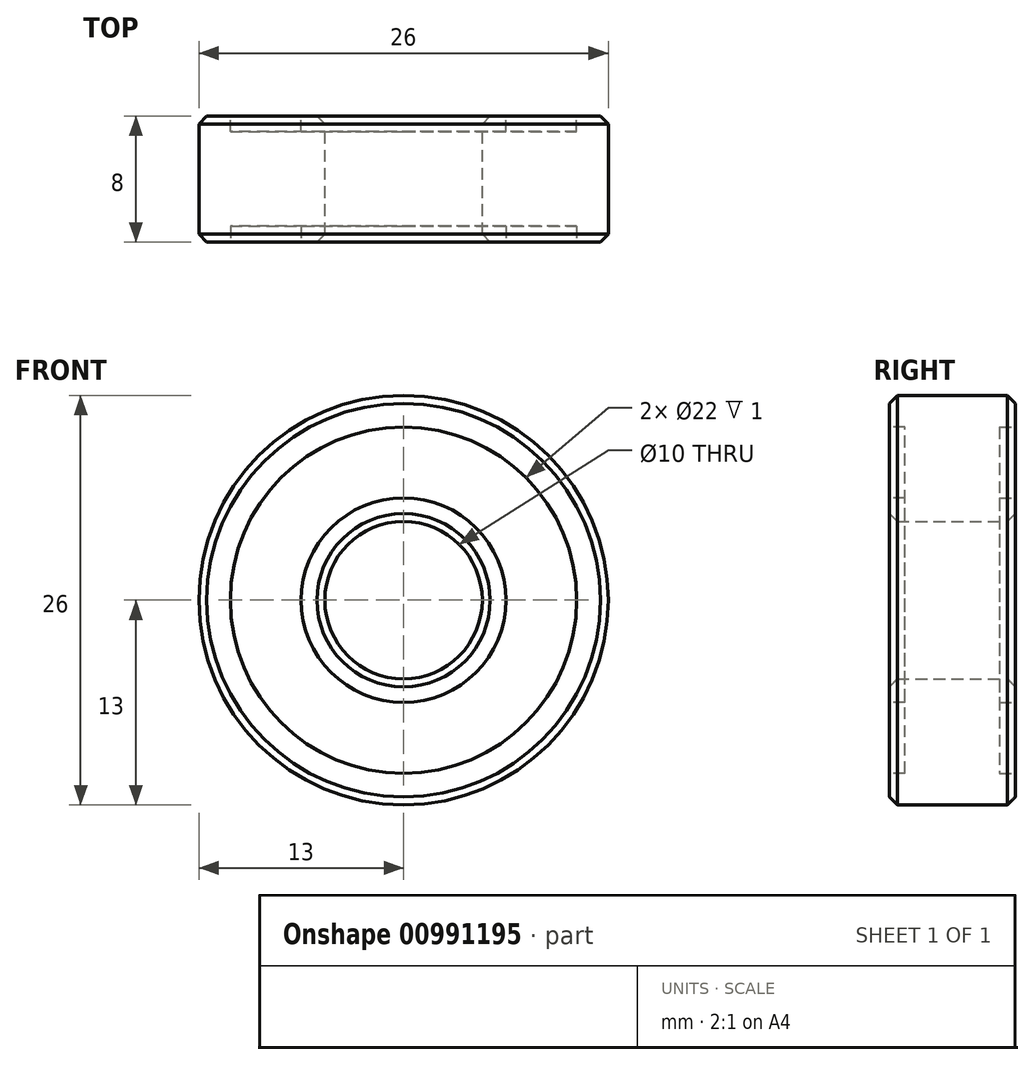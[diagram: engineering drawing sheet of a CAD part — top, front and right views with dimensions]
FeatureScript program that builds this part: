
annotation { "Feature Type Name" : "Feature", "Feature Type Description" : "" }
export const myFeature = defineFeature(function(context is Context, id is Id, definition is map)
    precondition{}
    {
        {
            var Q0;
            Q0=qCreatedBy(makeId("Front.planeOp"),FACE);
            var sketch = newSketch(context, id + "F0", { "sketchPlane" : qUnion([Q0])});
            skCircle(sketch, "E0", {"center": v(0, 0) * mm, "radius": 5 * mm});
            skCircle(sketch, "E1", {"center": v(0, 0) * mm, "radius": 13 * mm});
            skSolve(sketch);
        }
        {
            var Q0;
            Q0=makeQuery(id+"F0.imprint","IMPRINT",FACE,{"disambiguationData":[TD([[makeQuery(id+"F0.imprint","IMPRINT",EDGE,{"derivedFrom":sQuery(id+"F0.wireOp",EDGE,"E0")}),-1.0]])]});
            extrude(context, id + "F1", {"entities" : qUnion([Q0]), "depth" : 8 * mm, "offsetDistance" : 25 * mm, "symmetric" : true});
        }
        {
            var Q0;
            Q0=makeQuery(id+"F1.opExtrude","CAP_FACE",FACE,{"disambiguationData":[OSD([sQuery(id+"F0.wireOp",EDGE,"E0"),sQuery(id+"F0.wireOp",EDGE,"E1")])],"isStart":true});
            var sketch = newSketch(context, id + "F2", { "sketchPlane" : qUnion([Q0])});
            skCircle(sketch, "E2", {"center": v(0, 0) * mm, "radius": 6.5 * mm});
            skCircle(sketch, "E3", {"center": v(0, 0) * mm, "radius": 11 * mm});
            skSolve(sketch);
        }
        {
            var Q0;
            Q0=makeQuery(id+"F1.opExtrude","CAP_FACE",FACE,{"disambiguationData":[OSD([sQuery(id+"F0.wireOp",EDGE,"E0"),sQuery(id+"F0.wireOp",EDGE,"E1")])],"isStart":false});
            var sketch = newSketch(context, id + "F3", { "sketchPlane" : qUnion([Q0])});
            skCircle(sketch, "E4", {"center": v(0, 0) * mm, "radius": 6.5 * mm});
            skCircle(sketch, "E5", {"center": v(0, 0) * mm, "radius": 11 * mm});
            skSolve(sketch);
        }
        {
            var Q0;
            Q0=makeQuery(id+"F2.imprint","IMPRINT",FACE,{"disambiguationData":[TD([[makeQuery(id+"F2.imprint","IMPRINT",EDGE,{"derivedFrom":sQuery(id+"F2.wireOp",EDGE,"E2")}),-1.0]])]});
            extrude(context, id + "F4", {"entities" : qUnion([Q0]), "operationType" : NewBodyOperationType.REMOVE, "oppositeDirection" : true, "depth" : 1 * mm, "offsetDistance" : 25 * mm});
        }
        {
            var Q0;
            Q0=makeQuery(id+"F3.imprint","IMPRINT",FACE,{"disambiguationData":[TD([[makeQuery(id+"F3.imprint","IMPRINT",EDGE,{"derivedFrom":sQuery(id+"F3.wireOp",EDGE,"E4")}),-1.0]])]});
            extrude(context, id + "F5", {"entities" : qUnion([Q0]), "operationType" : NewBodyOperationType.REMOVE, "oppositeDirection" : true, "depth" : 1 * mm, "offsetDistance" : 25 * mm});
        }
        {
            var Q0;
            Q0=makeQuery(id+"F1.opExtrude","CAP_EDGE",EDGE,{"disambiguationData":[OSD([sQuery(id+"F0.wireOp",EDGE,"E1")])],"isStart":true});
            var Q1;
            Q1=makeQuery(id+"F1.opExtrude","CAP_EDGE",EDGE,{"disambiguationData":[OSD([sQuery(id+"F0.wireOp",EDGE,"E1")])],"isStart":false});
            var Q2;
            Q2=makeQuery(id+"F1.opExtrude","CAP_EDGE",EDGE,{"disambiguationData":[OSD([sQuery(id+"F0.wireOp",EDGE,"E0")])],"isStart":false});
            var Q3;
            Q3=makeQuery(id+"F1.opExtrude","CAP_EDGE",EDGE,{"disambiguationData":[OSD([sQuery(id+"F0.wireOp",EDGE,"E0")])],"isStart":true});
            var Q4;
            Q4=makeQuery(id+"F4.boolean.opBoolean","COPY",EDGE,{"derivedFrom":makeQuery(id+"F4.opExtrude","CAP_EDGE",EDGE,{"disambiguationData":[OSD([sQuery(id+"F2.wireOp",EDGE,"E2")])],"isStart":true})});
            var Q5;
            Q5=makeQuery(id+"F4.boolean.opBoolean","COPY",EDGE,{"derivedFrom":makeQuery(id+"F4.opExtrude","CAP_EDGE",EDGE,{"disambiguationData":[OSD([sQuery(id+"F2.wireOp",EDGE,"E3")])],"isStart":true})});
            var Q6;
            Q6=makeQuery(id+"F5.boolean.opBoolean","COPY",EDGE,{"derivedFrom":makeQuery(id+"F5.opExtrude","CAP_EDGE",EDGE,{"disambiguationData":[OSD([sQuery(id+"F3.wireOp",EDGE,"E5")])],"isStart":true})});
            var Q7;
            Q7=makeQuery(id+"F5.boolean.opBoolean","COPY",EDGE,{"derivedFrom":makeQuery(id+"F5.opExtrude","CAP_EDGE",EDGE,{"disambiguationData":[OSD([sQuery(id+"F3.wireOp",EDGE,"E4")])],"isStart":true})});
            chamfer(context, id + "F6", {"entities" : qUnion([Q0, Q1, Q2, Q3, Q4, Q5, Q6, Q7]), "width" : 0.5 * mm, "tangentPropagation" : true});
        }
    });
